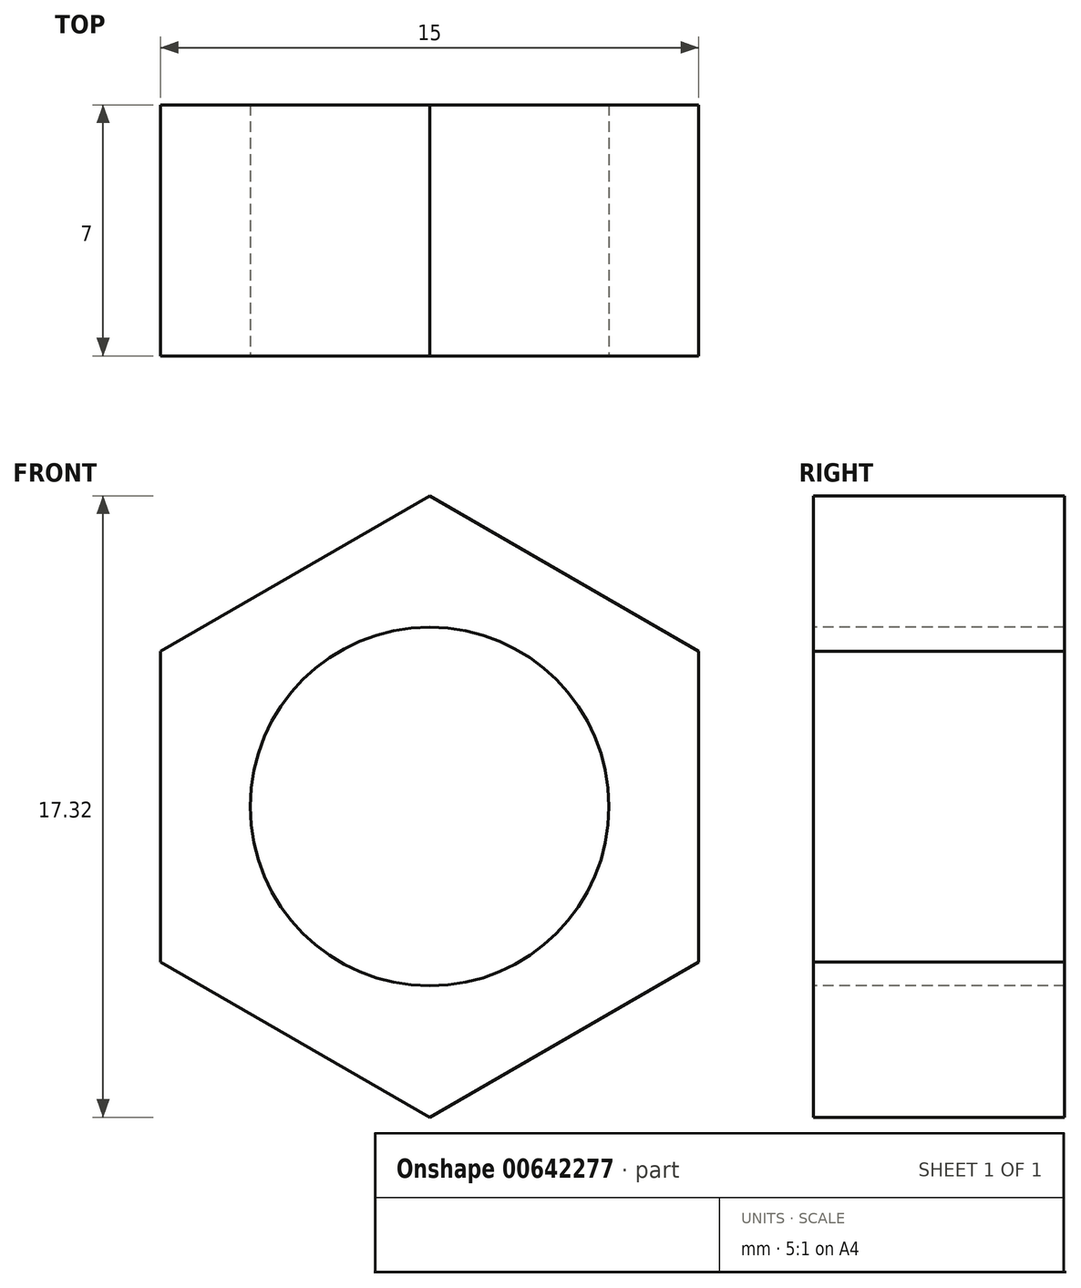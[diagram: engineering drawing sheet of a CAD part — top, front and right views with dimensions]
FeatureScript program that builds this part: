
annotation { "Feature Type Name" : "Feature", "Feature Type Description" : "" }
export const myFeature = defineFeature(function(context is Context, id is Id, definition is map)
    precondition{}
    {
        {
            var Q0;
            Q0=qCreatedBy(makeId("Front.planeOp"),FACE);
            var sketch = newSketch(context, id + "F0", { "sketchPlane" : qUnion([Q0])});
            skCircle(sketch, "E0.cCircle", {"center": v(0, 0) * mm, "radius": 7.5 * mm, "construction": true});
            skLineSegment(sketch, "E0.0", {"start": v(7.5, 4.33) * mm, "end": v(7.5, -4.33) * mm});
            skLineSegment(sketch, "E0.1", {"start": v(7.5, -4.33) * mm, "end": v(0, -8.66) * mm});
            skLineSegment(sketch, "E0.2", {"start": v(0, -8.66) * mm, "end": v(-7.5, -4.33) * mm});
            skLineSegment(sketch, "E0.3", {"start": v(-7.5, -4.33) * mm, "end": v(-7.5, 4.33) * mm});
            skLineSegment(sketch, "E0.4", {"start": v(-7.5, 4.33) * mm, "end": v(0, 8.66) * mm});
            skLineSegment(sketch, "E0.5", {"start": v(0, 8.66) * mm, "end": v(7.5, 4.33) * mm});
            skPoint(sketch, "E0.0.midPoint", {"position": v(7.5, 0) * mm});
            skSolve(sketch);
        }
        {
            var Q0;
            Q0=makeQuery(id+"F0.imprint","IMPRINT",FACE,{"disambiguationData":[TD([[makeQuery(id+"F0.imprint","IMPRINT",EDGE,{"derivedFrom":sQuery(id+"F0.wireOp",EDGE,"E0.0")}),-1.0]])]});
            extrude(context, id + "F1", {"entities" : qUnion([Q0]), "depth" : 7 * mm, "offsetDistance" : 25 * mm});
        }
        {
            var Q0;
            Q0=makeQuery(id+"F1.opExtrude","CAP_FACE",FACE,{"disambiguationData":[OSD([sQuery(id+"F0.wireOp",EDGE,"E0.0"),sQuery(id+"F0.wireOp",EDGE,"E0.1"),sQuery(id+"F0.wireOp",EDGE,"E0.2"),sQuery(id+"F0.wireOp",EDGE,"E0.3"),sQuery(id+"F0.wireOp",EDGE,"E0.4"),sQuery(id+"F0.wireOp",EDGE,"E0.5")])],"isStart":false});
            var sketch = newSketch(context, id + "F2", { "sketchPlane" : qUnion([Q0])});
            skPoint(sketch, "E1", {"position": v(0, 0) * mm});
            skSolve(sketch);
        }
        {
            var Q0;
            Q0=sQuery(id+"F2.wireOp",VERTEX,"E1");
            var Q1;
            Q1=makeQuery(id+"F1.opExtrude","SWEPT_BODY",BODY,{"disambiguationData":[OSD([sQuery(id+"F0.wireOp",EDGE,"E0.0"),sQuery(id+"F0.wireOp",EDGE,"E0.1"),sQuery(id+"F0.wireOp",EDGE,"E0.2"),sQuery(id+"F0.wireOp",EDGE,"E0.3"),sQuery(id+"F0.wireOp",EDGE,"E0.4"),sQuery(id+"F0.wireOp",EDGE,"E0.5")])]});
            hole(context, id + "F3", {"style" : HoleStyle.SIMPLE, "endStyle" : HoleEndStyle.THROUGH, "holeDiameter" : 10 * mm, "majorDiameter" : 5 * mm, "isTappedThrough" : true, "tappedDepth" : 12 * mm, "tapClearance" : 3, "locations" : qUnion([Q0]), "scope" : qUnion([Q1])});
        }
    });
